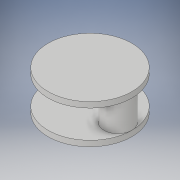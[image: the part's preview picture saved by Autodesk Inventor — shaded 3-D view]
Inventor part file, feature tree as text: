
AUTODESK INVENTOR PART (.ipt)
format: ipt  version: 2018 (Build 220112000, 112)  size: 108,544 bytes
history: native  units: in
note: dims shown in document units (in); Inventor stores cm internally (conversion verified against a paired STEP export)
features: extrude x3, sketch x3, projected_geometry x1
ambient origin geometry x8: Origin, YZ Plane, XZ Plane, XY Plane, X Axis, Y Axis, Z Axis, Center Point
bodies: Solid1 (feature_tree)
feature tree (7):
  extrude  "Extrusion1"  Depth=0.1in TaperAngle=0.0deg
  extrude  "Extrusion2"  Depth=0.5in
  extrude  "Extrusion3"  Depth=0.1in TaperAngle=0.0deg
  sketch  "Sketch1"  dims[d0=1.5in d1=0.1in d2=0.0in]
  sketch  "Sketch2"  dims[d3=0.5in d4=0.5in]
  sketch  "Sketch3"  dims[d5=0.5in d6=0.0in d7=0.1in d8=0.0in]
  projected_geometry  "Projected Loop1"
